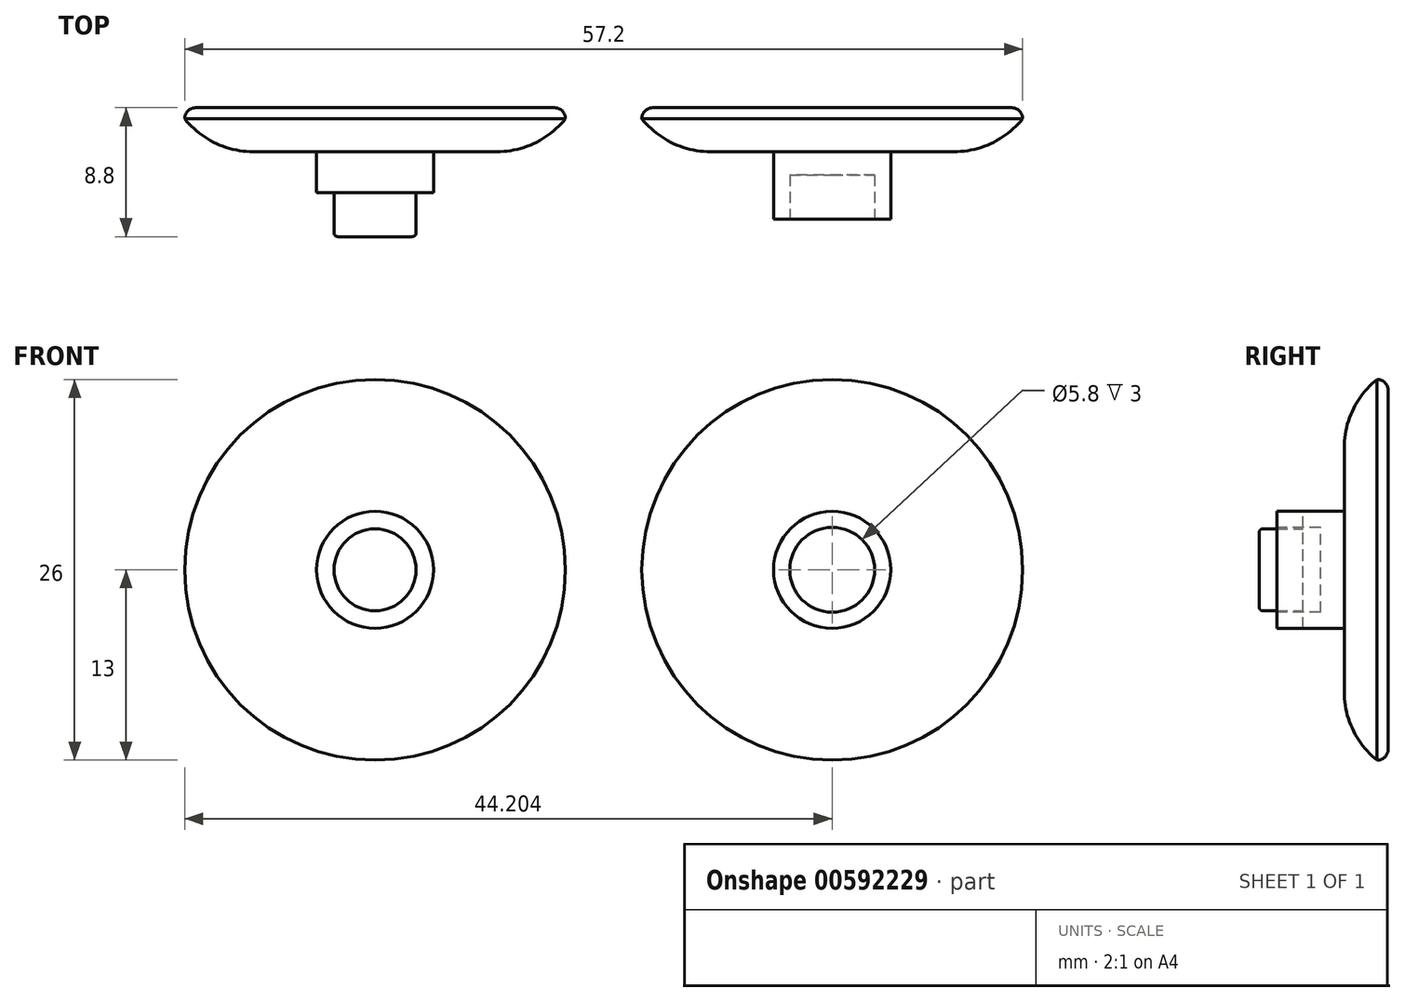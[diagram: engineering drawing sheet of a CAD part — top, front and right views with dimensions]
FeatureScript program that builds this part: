
annotation { "Feature Type Name" : "Feature", "Feature Type Description" : "" }
export const myFeature = defineFeature(function(context is Context, id is Id, definition is map)
    precondition{}
    {
        {
            var Q0;
            Q0=qCreatedBy(makeId("Front.planeOp"),FACE);
            var sketch = newSketch(context, id + "F0", { "sketchPlane" : qUnion([Q0])});
            skCircle(sketch, "E0", {"center": v(0, 0) * mm, "radius": 13 * mm});
            skSolve(sketch);
        }
        {
            var Q0;
            Q0=makeQuery(id+"F0.imprint","IMPRINT",FACE,{"disambiguationData":[TD([[makeQuery(id+"F0.imprint","IMPRINT",EDGE,{"derivedFrom":sQuery(id+"F0.wireOp",EDGE,"E0")}),1.0]])]});
            extrude(context, id + "F1", {"entities" : qUnion([Q0]), "depth" : 3 * mm, "offsetDistance" : 25 * mm});
        }
        {
            var Q0;
            Q0=makeQuery(id+"F1.opExtrude","CAP_FACE",FACE,{"disambiguationData":[OSD([sQuery(id+"F0.wireOp",EDGE,"E0")])],"isStart":false});
            var sketch = newSketch(context, id + "F2", { "sketchPlane" : qUnion([Q0])});
            skCircle(sketch, "E1", {"center": v(0, 0) * mm, "radius": 4 * mm});
            skSolve(sketch);
        }
        {
            var Q0;
            Q0=makeQuery(id+"F2.imprint","IMPRINT",FACE,{"disambiguationData":[TD([[makeQuery(id+"F2.imprint","IMPRINT",EDGE,{"derivedFrom":sQuery(id+"F2.wireOp",EDGE,"E1")}),1.0]])]});
            extrude(context, id + "F3", {"entities" : qUnion([Q0]), "operationType" : NewBodyOperationType.ADD, "depth" : 2.8 * mm, "offsetDistance" : 25 * mm});
        }
        {
            var Q0;
            Q0=makeQuery(id+"F3.opExtrude","CAP_FACE",FACE,{"disambiguationData":[OSD([sQuery(id+"F2.wireOp",EDGE,"E1")])],"isStart":false});
            var sketch = newSketch(context, id + "F4", { "sketchPlane" : qUnion([Q0])});
            skCircle(sketch, "E2", {"center": v(0, 0) * mm, "radius": 2.8 * mm});
            skSolve(sketch);
        }
        {
            var Q0;
            Q0=makeQuery(id+"F4.imprint","IMPRINT",FACE,{"disambiguationData":[TD([[makeQuery(id+"F4.imprint","IMPRINT",EDGE,{"derivedFrom":sQuery(id+"F4.wireOp",EDGE,"E2")}),1.0]])]});
            extrude(context, id + "F5", {"entities" : qUnion([Q0]), "operationType" : NewBodyOperationType.ADD, "depth" : 3 * mm, "offsetDistance" : 25 * mm});
        }
        {
            var Q0;
            Q0=qCreatedBy(makeId("Front.planeOp"),FACE);
            var sketch = newSketch(context, id + "F6", { "sketchPlane" : qUnion([Q0])});
            skCircle(sketch, "E3", {"center": v(31.2, 0) * mm, "radius": 13 * mm});
            skSolve(sketch);
        }
        {
            var Q0;
            Q0=makeQuery(id+"F6.imprint","IMPRINT",FACE,{"disambiguationData":[TD([[makeQuery(id+"F6.imprint","IMPRINT",EDGE,{"derivedFrom":sQuery(id+"F6.wireOp",EDGE,"E3")}),1.0]])]});
            extrude(context, id + "F7", {"entities" : qUnion([Q0]), "depth" : 3 * mm, "offsetDistance" : 25 * mm});
        }
        {
            var Q0;
            Q0=makeQuery(id+"F7.opExtrude","CAP_FACE",FACE,{"disambiguationData":[OSD([sQuery(id+"F6.wireOp",EDGE,"E3")])],"isStart":false});
            var sketch = newSketch(context, id + "F8", { "sketchPlane" : qUnion([Q0])});
            skCircle(sketch, "E4", {"center": v(31.2, 0) * mm, "radius": 4 * mm});
            skSolve(sketch);
        }
        {
            var Q0;
            Q0=makeQuery(id+"F8.imprint","IMPRINT",FACE,{"disambiguationData":[TD([[makeQuery(id+"F8.imprint","IMPRINT",EDGE,{"derivedFrom":sQuery(id+"F8.wireOp",EDGE,"E4")}),1.0]])]});
            extrude(context, id + "F9", {"entities" : qUnion([Q0]), "operationType" : NewBodyOperationType.ADD, "depth" : 4.6 * mm, "offsetDistance" : 25 * mm});
        }
        {
            var Q0;
            Q0=makeQuery(id+"F9.opExtrude","CAP_FACE",FACE,{"disambiguationData":[OSD([sQuery(id+"F8.wireOp",EDGE,"E4")])],"isStart":false});
            var sketch = newSketch(context, id + "F10", { "sketchPlane" : qUnion([Q0])});
            skCircle(sketch, "E5", {"center": v(31.2, 0) * mm, "radius": 2.9 * mm});
            skSolve(sketch);
        }
        {
            var Q0;
            Q0=makeQuery(id+"F10.imprint","IMPRINT",FACE,{"disambiguationData":[TD([[makeQuery(id+"F10.imprint","IMPRINT",EDGE,{"derivedFrom":sQuery(id+"F10.wireOp",EDGE,"E5")}),1.0]])]});
            extrude(context, id + "F11", {"entities" : qUnion([Q0]), "operationType" : NewBodyOperationType.REMOVE, "oppositeDirection" : true, "depth" : 3 * mm, "offsetDistance" : 25 * mm});
        }
        {
            var Q0;
            Q0=makeQuery(id+"F7.opExtrude","CAP_EDGE",EDGE,{"disambiguationData":[OSD([sQuery(id+"F6.wireOp",EDGE,"E3")])],"isStart":true});
            var Q1;
            Q1=makeQuery(id+"F1.opExtrude","CAP_EDGE",EDGE,{"disambiguationData":[OSD([sQuery(id+"F0.wireOp",EDGE,"E0")])],"isStart":true});
            fillet(context, id + "F12", {"entities" : qUnion([Q0, Q1]), "radius" : .75 * mm, "tangentPropagation" : true, "allowEdgeOverflow" : false});
        }
        {
            var Q0;
            Q0=makeQuery(id+"F11.boolean.opBoolean","COPY",EDGE,{"derivedFrom":makeQuery(id+"F11.opExtrude","CAP_EDGE",EDGE,{"disambiguationData":[OSD([sQuery(id+"F10.wireOp",EDGE,"E5")])],"isStart":true})});
            var Q1;
            Q1=makeQuery(id+"F5.opExtrude","CAP_EDGE",EDGE,{"disambiguationData":[OSD([sQuery(id+"F4.wireOp",EDGE,"E2")])],"isStart":false});
            fillet(context, id + "F13", {"entities" : qUnion([Q0, Q1]), "radius" : .25 * mm, "tangentPropagation" : true, "allowEdgeOverflow" : false});
        }
        {
            var Q0;
            Q0=makeQuery(id+"F7.opExtrude","CAP_EDGE",EDGE,{"disambiguationData":[OSD([sQuery(id+"F6.wireOp",EDGE,"E3")])],"isStart":false});
            var Q1;
            Q1=makeQuery(id+"F1.opExtrude","CAP_EDGE",EDGE,{"disambiguationData":[OSD([sQuery(id+"F0.wireOp",EDGE,"E0")])],"isStart":false});
            fillet(context, id + "F14", {"entities" : qUnion([Q0, Q1]), "radius" : 6 * mm, "allowEdgeOverflow" : false});
        }
    });
